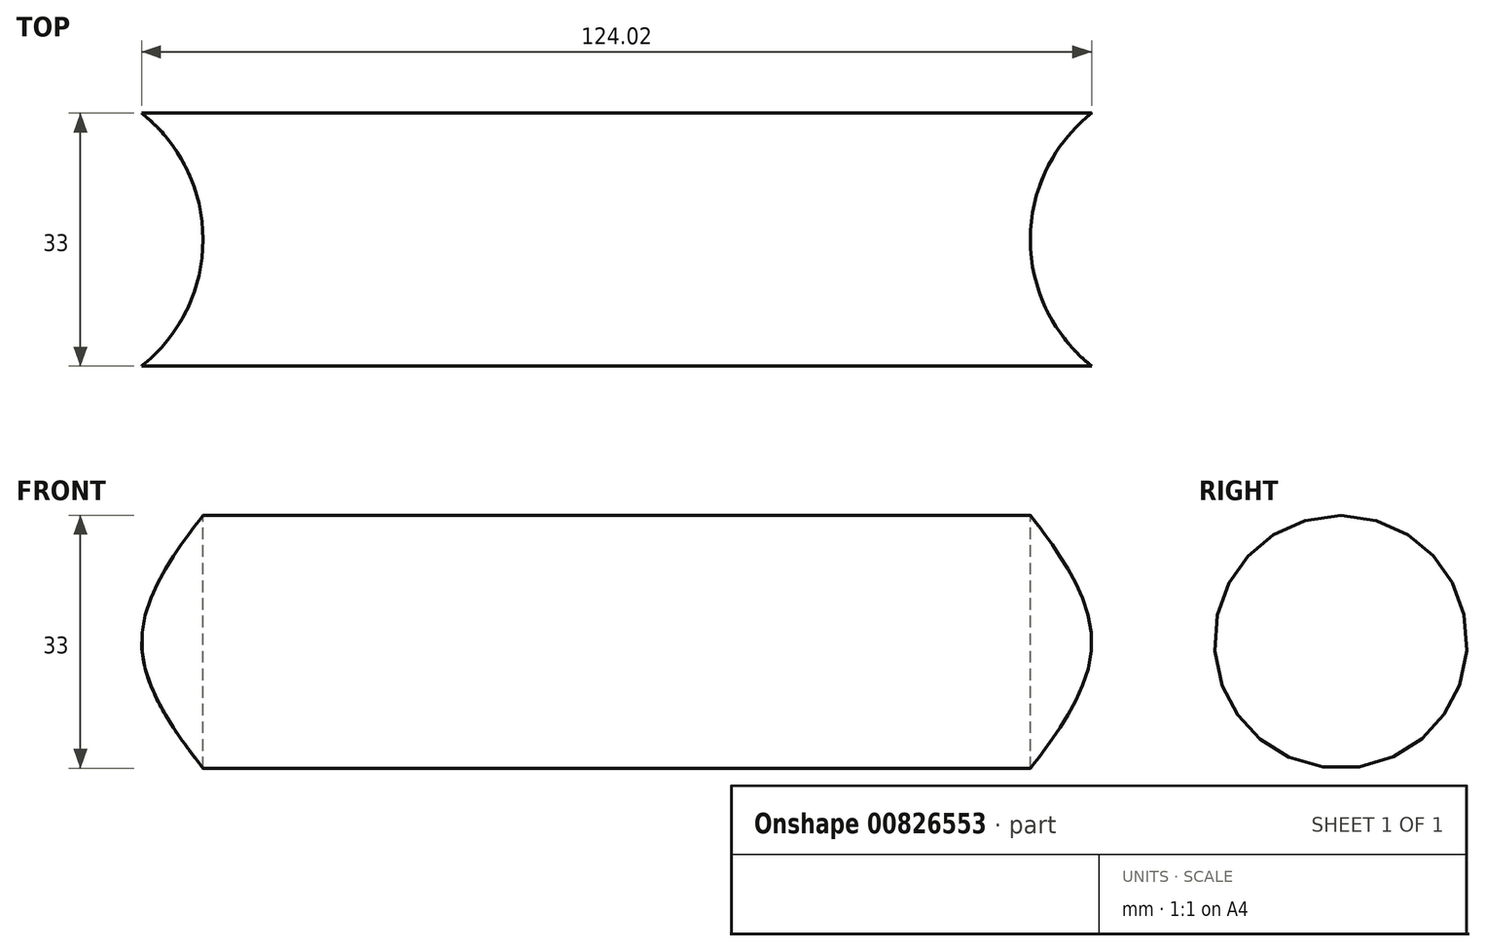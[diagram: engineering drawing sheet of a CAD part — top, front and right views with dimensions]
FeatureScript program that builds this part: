
annotation { "Feature Type Name" : "Feature", "Feature Type Description" : "" }
export const myFeature = defineFeature(function(context is Context, id is Id, definition is map)
    precondition{}
    {
        {
            var Q0;
            Q0=qCreatedBy(makeId("Right.planeOp"),FACE);
            var sketch = newSketch(context, id + "F0", { "sketchPlane" : qUnion([Q0])});
            skCircle(sketch, "E0", {"center": v(0, 0) * mm, "radius": 16.5 * mm});
            skSolve(sketch);
        }
        {
            var Q0;
            Q0=makeQuery(id+"F0.imprint","IMPRINT",FACE,{"disambiguationData":[TD([[makeQuery(id+"F0.imprint","IMPRINT",EDGE,{"derivedFrom":sQuery(id+"F0.wireOp",EDGE,"E0")}),1.0]])]});
            extrude(context, id + "F1", {"entities" : qUnion([Q0]), "depth" : 150 * mm, "offsetDistance" : 25 * mm});
        }
        {
            var Q0;
            Q0=qCreatedBy(makeId("Top.planeOp"),FACE);
            var sketch = newSketch(context, id + "F2", { "sketchPlane" : qUnion([Q0])});
            skCircle(sketch, "E1", {"center": v(0, 0) * mm, "radius": 21 * mm});
            skLineSegment(sketch, "E2", {"start": v(0, 0) * mm, "end": v(150, 0) * mm});
            skCircle(sketch, "E3", {"center": v(150, 0) * mm, "radius": 21 * mm});
            skSolve(sketch);
        }
        {
            var Q0;
            Q0=makeQuery(id+"F2.imprint","IMPRINT",FACE,{"disambiguationData":[TD([[makeQuery(id+"F2.imprint","IMPRINT",EDGE,{"derivedFrom":sQuery(id+"F2.wireOp",EDGE,"E3")}),1.0]])]});
            var Q1;
            Q1=makeQuery(id+"F2.imprint","IMPRINT",FACE,{"disambiguationData":[TD([[makeQuery(id+"F2.imprint","IMPRINT",EDGE,{"derivedFrom":sQuery(id+"F2.wireOp",EDGE,"E1")}),1.0]])]});
            extrude(context, id + "F3", {"entities" : qUnion([Q0, Q1]), "operationType" : NewBodyOperationType.REMOVE, "endBound" : BoundingType.SYMMETRIC, "oppositeDirection" : true, "depth" : 200 * mm, "offsetDistance" : 25 * mm});
        }
    });
